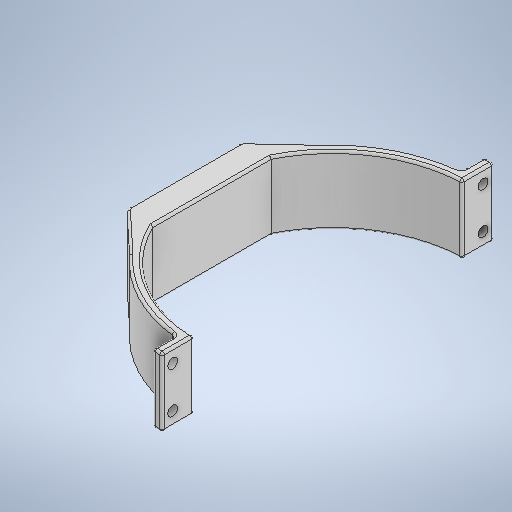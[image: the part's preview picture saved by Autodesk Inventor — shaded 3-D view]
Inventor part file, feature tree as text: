
AUTODESK INVENTOR PART (.ipt)
format: ipt  version: 2025.1 (Build 291241000, 241)  size: 390,144 bytes
history: native  units: mm
features: fillet x3, extrude x2, sketch x2
ambient origin geometry x8: Origin, YZ Plane, XZ Plane, XY Plane, X Axis, Y Axis, Z Axis, Center Point
bodies: Solide1 (feature_tree)
feature tree (7):
  extrude  "Extrusion1"  Depth=125.48mm
  fillet  "Congé2"  Radius=117.383mm
  fillet  "Congé3"  Radius=2.0mm
  fillet  "Congé4"  Radius=4.0mm
  extrude  "Extrusion2"  Depth=144.917mm
  sketch  "Esquisse1"
  sketch  "Esquisse2"
